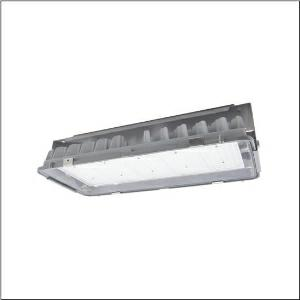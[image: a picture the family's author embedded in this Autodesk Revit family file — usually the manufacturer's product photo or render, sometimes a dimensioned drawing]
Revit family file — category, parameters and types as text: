
# Revit family: highbay_11xtreme_51hf61da4hma
name_source: partatom
category: Lighting Fixtures
units: mm (PartAtom-declared; Revit-internal decimal feet)

## family parameters
Cut with Voids When Loaded = No
Host = Face
Light Source = No
Part Type = Normal
Room Calculation Point = No
Round Connector Dimension = Use Diameter
Shared = No

## types (1)
- --- (1 x LED, 18700 lm, 96.3 W, 4000K)
    Apparent Load = 96 VA
    CIE Flux Codes = 88 96 99 100 100
    Color Rendering = 80
    Color Temperature = 4000K
    Default Elevation = 1800 mm
    Description = Highbay 11Xtreme, high bay luminaire, primary light control with lens, of PMMA, primary optical cover: cover, of toughened safety glass, light emission: direct distribution, primary light characteristic: symmetric, installation type: suspended mounting, surface-mounted, 1x LED module,for 1x LED, rated luminous flux: 18.700lm, luminous efficacy: 194lm/W, light colour: 840, colour temperature: 4000K, control gear: DALI 2, with cable H07RN-F 5x 1.5mm², mains connection: 220..240V, AC, 50/60Hz, cable length: 1,5m, rated input power: 96W, luminaire housing, of diecast aluminium, coated, silver, length: 595mm, width: 280mm, height: 195mm, protection rating (complete): IP66, insulation class (complete): insulation class I (protective earthing), certification: CE, ENEC, UKCA, protection symbol: D, ball protection: ball impact resistant according to DIN VDE 0710 part 13 (with chain suspension), impact resistance: IK08, permissible operating ambient temperature: -25..+70°C, reducing of maximum allowable ambient temperature of 5°C with ceiling mounting, packaging unit: 1 piece
    Height = 157 mm
    Lamp = 1 x LED
    Lamp Light Flux = 18700 lm
    Lamp Power = 96.3 W
    Lamp count = 1
    Length = 593 mm
    Luminous efficacy = 194 lm/W
    Manufacturer = Siteco
    ModVariant = No
    Model = 51HF61DA4HMA
    Mounting Place = Ceiling
    Mounting Type = Pendant
    Number of Poles = 1
    OnlyDefault = Yes
    Power Factor = 1
    Product Name = Highbay 11Xtreme
    Product group = high bay luminaire
    ProductGroupID = 901
    Protection Class = Protection class I
    Protection Degree = IP 66
    RLX_Detail_Level = 1
    RLX_Emergency_Light_Flux = 0 lm
    RLX_Emergency_Type = 0
    RLX_Emergency_Type_DB = No
    RlxData = <blob elided: 27753 chars, md5=21ceab3d>
    Socket = socket
    Standby Power = 0 W
    System Light Flux = 18700 lm
    System Power = 96 W
    Type Comments = factory setting: luminous flux: 100 % | dim-lin: 254 | 650 mA
    Type Image = l_1258342.jpg
    URL = http://relux.com
    VarID = @adj_083572
    Voltage = 0 V
    Weight = 0.00 kg
    Width = 278 mm

## geometry (parser evidence)
native form markers: Blend x4, Sweep x12
no freeform markers — native parametric forms only
